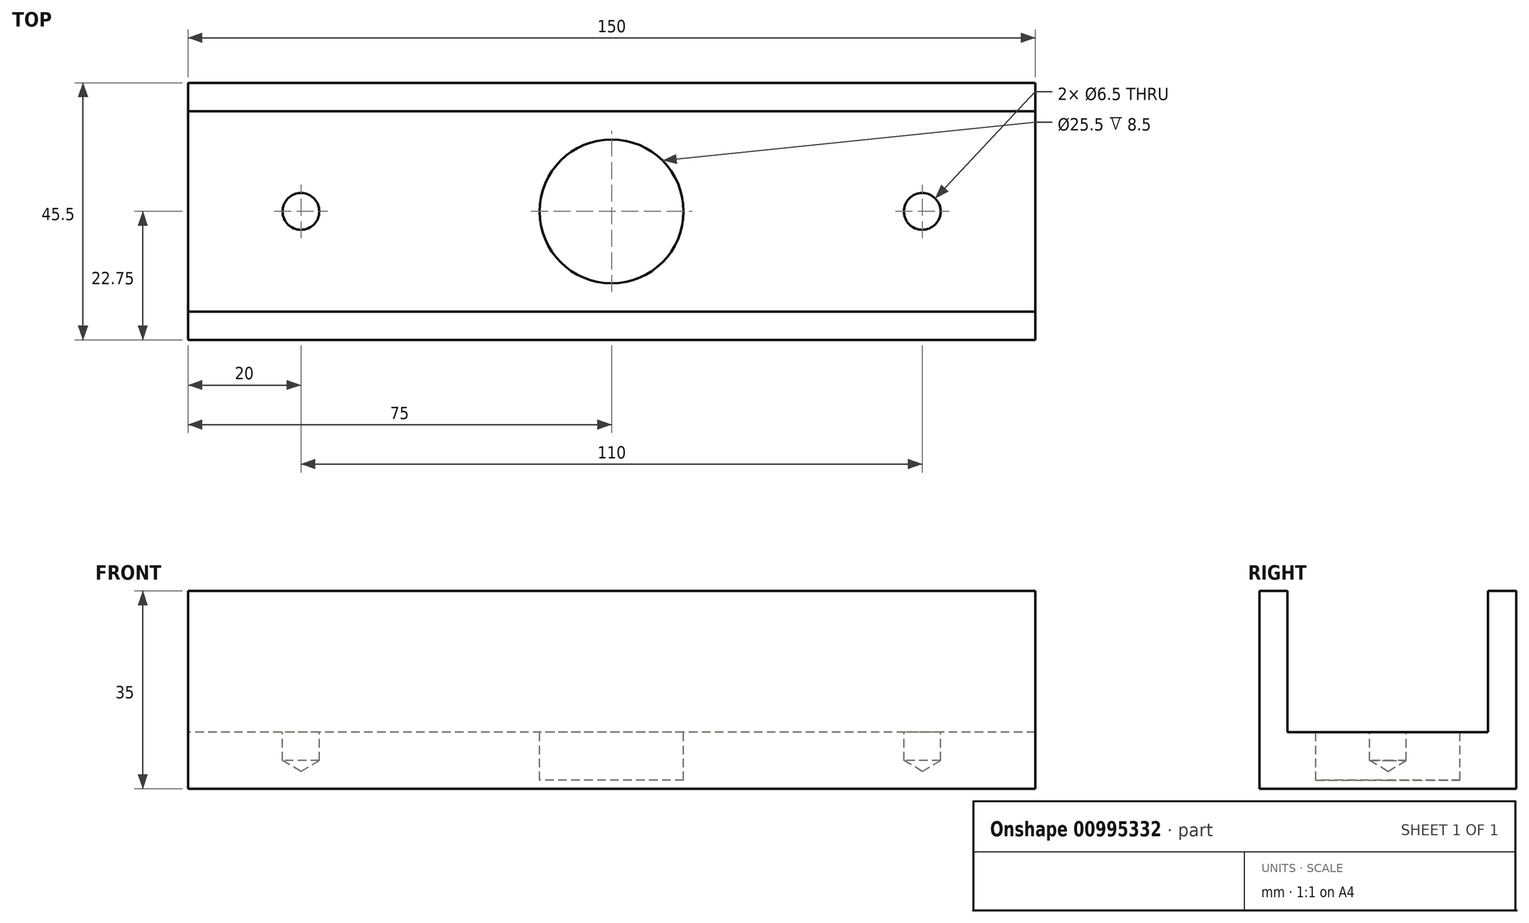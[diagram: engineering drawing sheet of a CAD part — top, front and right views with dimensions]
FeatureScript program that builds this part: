
annotation { "Feature Type Name" : "Feature", "Feature Type Description" : "" }
export const myFeature = defineFeature(function(context is Context, id is Id, definition is map)
    precondition{}
    {
        {
            var Q0;
            Q0=qCreatedBy(makeId("Top.planeOp"),FACE);
            var sketch = newSketch(context, id + "F0", { "sketchPlane" : qUnion([Q0])});
            skLineSegment(sketch, "E0.bottom", {"start": v(75, 22.75) * mm, "end": v(-75, 22.75) * mm});
            skLineSegment(sketch, "E0.top", {"start": v(75, -22.75) * mm, "end": v(-75, -22.75) * mm});
            skLineSegment(sketch, "E0.left", {"start": v(75, 22.75) * mm, "end": v(75, -22.75) * mm});
            skLineSegment(sketch, "E0.right", {"start": v(-75, 22.75) * mm, "end": v(-75, -22.75) * mm});
            skPoint(sketch, "E0.middle", {"position": v(0, 0) * mm});
            skSolve(sketch);
        }
        {
            var Q0;
            Q0 = qSketchRegion(id + "F0", true);
            extrude(context, id + "F1", {"entities" : qUnion([Q0]), "depth" : 35 * mm, "offsetDistance" : 25 * mm});
        }
        {
            var Q0;
            Q0=makeQuery(id+"F1.opExtrude","CAP_FACE",FACE,{"disambiguationData":[OSD([sQuery(id+"F0.wireOp",EDGE,"E0.bottom"),sQuery(id+"F0.wireOp",EDGE,"E0.top"),sQuery(id+"F0.wireOp",EDGE,"E0.left"),sQuery(id+"F0.wireOp",EDGE,"E0.right")])],"isStart":false});
            var sketch = newSketch(context, id + "F2", { "sketchPlane" : qUnion([Q0])});
            skLineSegment(sketch, "E1.0", {"start": v(75, 17.75) * mm, "end": v(-75, 17.75) * mm});
            skLineSegment(sketch, "E2.0", {"start": v(75, -17.75) * mm, "end": v(-75, -17.75) * mm});
            skSolve(sketch);
        }
        {
            var Q0;
            {var subQ0=sQuery(id+"F2.wireOp",EDGE,"E1.0");Q0=makeQuery(id+"F2.imprint","IMPRINT",FACE,{"disambiguationData":[TD([[makeQuery(id+"F2.imprint","IMPRINT",EDGE,{"derivedFrom":subQ0}),1.0]])]});}
            extrude(context, id + "F3", {"entities" : qUnion([Q0]), "operationType" : NewBodyOperationType.REMOVE, "oppositeDirection" : true, "depth" : 25 * mm, "offsetDistance" : 25 * mm});
        }
        {
            var Q0;
            Q0=makeQuery(id+"F3.boolean.opBoolean","COPY",FACE,{"derivedFrom":makeQuery(id+"F3.opExtrude","CAP_FACE",FACE,{"disambiguationData":[OSD([sQuery(id+"F0.wireOp",EDGE,"E0.left"),sQuery(id+"F0.wireOp",EDGE,"E0.right"),sQuery(id+"F2.wireOp",EDGE,"E1.0"),sQuery(id+"F2.wireOp",EDGE,"E2.0")])],"isStart":false})});
            var sketch = newSketch(context, id + "F4", { "sketchPlane" : qUnion([Q0])});
            skPoint(sketch, "E3", {"position": v(-55, 0) * mm});
            skPoint(sketch, "E4", {"position": v(55, 0) * mm});
            skCircle(sketch, "E5", {"center": v(0, 0) * mm, "radius": 12.75 * mm});
            skSolve(sketch);
        }
        {
            var Q0;
            Q0=makeQuery(id+"F4.imprint","IMPRINT",FACE,{"disambiguationData":[TD([[makeQuery(id+"F4.imprint","IMPRINT",EDGE,{"derivedFrom":sQuery(id+"F4.wireOp",EDGE,"E5")}),1.0]])]});
            extrude(context, id + "F5", {"entities" : qUnion([Q0]), "operationType" : NewBodyOperationType.REMOVE, "oppositeDirection" : true, "depth" : 8.5 * mm, "offsetDistance" : 25 * mm});
        }
        {
            var Q0;
            Q0=sQuery(id+"F4.wireOp",VERTEX,"E4");
            var Q1;
            Q1=sQuery(id+"F4.wireOp",VERTEX,"E3");
            var Q2;
            Q2=makeQuery(id+"F1.opExtrude","SWEPT_BODY",BODY,{"disambiguationData":[OSD([sQuery(id+"F0.wireOp",EDGE,"E0.bottom"),sQuery(id+"F0.wireOp",EDGE,"E0.top"),sQuery(id+"F0.wireOp",EDGE,"E0.left"),sQuery(id+"F0.wireOp",EDGE,"E0.right")])]});
            hole(context, id + "F6", {"style" : HoleStyle.SIMPLE, "endStyle" : HoleEndStyle.BLIND, "holeDiameter" : 6.5 * mm, "majorDiameter" : 5 * mm, "holeDepth" : 5 * mm, "isTappedThrough" : true, "tappedDepth" : 12 * mm, "tapClearance" : 3, "locations" : qUnion([Q0, Q1]), "scope" : qUnion([Q2])});
        }
    });
